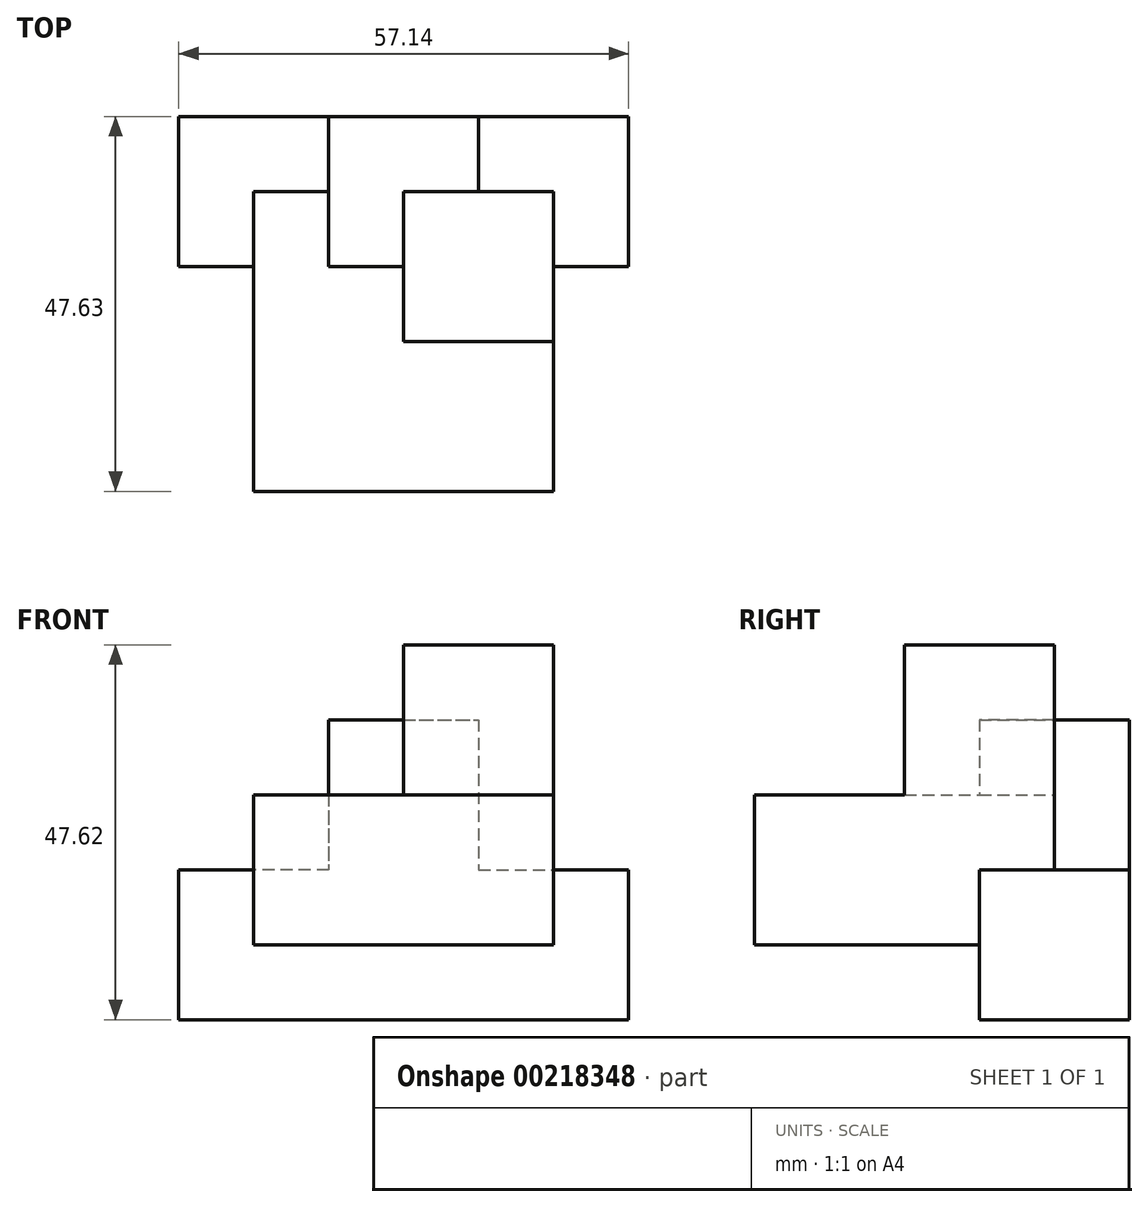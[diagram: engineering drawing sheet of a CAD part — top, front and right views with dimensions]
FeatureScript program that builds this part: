
annotation { "Feature Type Name" : "Feature", "Feature Type Description" : "" }
export const myFeature = defineFeature(function(context is Context, id is Id, definition is map)
    precondition{}
    {
        {
            var Q0;
            Q0=qCreatedBy(makeId("Front.planeOp"),FACE);
            var sketch = newSketch(context, id + "F0", { "sketchPlane" : qUnion([Q0])});
            skLineSegment(sketch, "E0.bottom", {"start": v(-9.52, 9.52) * mm, "end": v(9.53, 9.52) * mm});
            skLineSegment(sketch, "E0.top", {"start": v(-9.53, -9.53) * mm, "end": v(9.53, -9.53) * mm});
            skLineSegment(sketch, "E0.left", {"start": v(-9.53, 9.53) * mm, "end": v(-9.53, -9.53) * mm});
            skLineSegment(sketch, "E0.right", {"start": v(9.53, 9.53) * mm, "end": v(9.53, -9.53) * mm});
            skPoint(sketch, "E0.middle", {"position": v(0, 0) * mm});
            skLineSegment(sketch, "E1.bottom", {"start": v(-9.53, -9.53) * mm, "end": v(9.52, -9.53) * mm});
            skLineSegment(sketch, "E1.top", {"start": v(-9.53, -28.58) * mm, "end": v(9.53, -28.58) * mm});
            skLineSegment(sketch, "E1.left", {"start": v(-9.53, -9.53) * mm, "end": v(-9.53, -28.58) * mm});
            skLineSegment(sketch, "E1.right", {"start": v(9.52, -9.53) * mm, "end": v(9.52, -28.58) * mm});
            skLineSegment(sketch, "E2.bottom", {"start": v(-9.53, -9.53) * mm, "end": v(-28.58, -9.53) * mm});
            skLineSegment(sketch, "E2.top", {"start": v(-9.53, -28.58) * mm, "end": v(-28.57, -28.58) * mm});
            skLineSegment(sketch, "E2.right", {"start": v(-28.58, -9.53) * mm, "end": v(-28.57, -28.58) * mm});
            skLineSegment(sketch, "E3.bottom", {"start": v(9.53, -9.53) * mm, "end": v(28.57, -9.53) * mm});
            skLineSegment(sketch, "E3.top", {"start": v(9.53, -28.58) * mm, "end": v(28.57, -28.58) * mm});
            skLineSegment(sketch, "E3.left", {"start": v(9.53, -9.53) * mm, "end": v(9.53, -28.58) * mm});
            skLineSegment(sketch, "E3.right", {"start": v(28.57, -9.52) * mm, "end": v(28.57, -28.58) * mm});
            skSolve(sketch);
        }
        {
            var Q0;
            Q0=makeQuery(id+"F0.imprint","IMPRINT",FACE,{"disambiguationData":[TD([[makeQuery(id+"F0.imprint","IMPRINT",EDGE,{"derivedFrom":sQuery(id+"F0.wireOp",EDGE,"E0.bottom")}),-1.0]])]});
            var Q1;
            Q1=makeQuery(id+"F0.imprint","IMPRINT",FACE,{"disambiguationData":[TD([[makeQuery(id+"F0.imprint","IMPRINT",EDGE,{"derivedFrom":sQuery(id+"F0.wireOp",EDGE,"E2.bottom")}),1.0]])]});
            var Q2;
            Q2=makeQuery(id+"F0.imprint","IMPRINT",FACE,{"disambiguationData":[TD([[makeQuery(id+"F0.imprint","IMPRINT",EDGE,{"derivedFrom":sQuery(id+"F0.wireOp",EDGE,"E1.bottom")}),-1.0]])]});
            var Q3;
            Q3=makeQuery(id+"F0.imprint","IMPRINT",FACE,{"disambiguationData":[TD([[makeQuery(id+"F0.imprint","IMPRINT",EDGE,{"derivedFrom":sQuery(id+"F0.wireOp",EDGE,"E3.bottom")}),-1.0]])]});
            extrude(context, id + "F1", {"entities" : qUnion([Q0, Q1, Q2, Q3]), "endBound" : BoundingType.SYMMETRIC, "depth" : 19.05 * mm});
        }
        {
            var Q0;
            Q0=qCreatedBy(makeId("Front.planeOp"),FACE);
            var sketch = newSketch(context, id + "F2", { "sketchPlane" : qUnion([Q0])});
            skLineSegment(sketch, "E4.bottom", {"start": v(0, 0) * mm, "end": v(-19.05, 0) * mm});
            skLineSegment(sketch, "E4.left", {"start": v(0, 0) * mm, "end": v(0, 19.05) * mm});
            skLineSegment(sketch, "E5.top", {"start": v(0, -19.05) * mm, "end": v(-19.05, -19.05) * mm});
            skLineSegment(sketch, "E5.left", {"start": v(0, 0) * mm, "end": v(0, -19.05) * mm});
            skLineSegment(sketch, "E5.right", {"start": v(-19.05, 0) * mm, "end": v(-19.05, -19.05) * mm});
            skLineSegment(sketch, "E6.bottom", {"start": v(0, 0) * mm, "end": v(19.05, 0) * mm});
            skLineSegment(sketch, "E6.top", {"start": v(0, 19.05) * mm, "end": v(19.05, 19.05) * mm});
            skLineSegment(sketch, "E6.right", {"start": v(19.05, 0) * mm, "end": v(19.05, 19.05) * mm});
            skLineSegment(sketch, "E7.top", {"start": v(0, -19.05) * mm, "end": v(19.05, -19.05) * mm});
            skLineSegment(sketch, "E7.right", {"start": v(19.05, 0) * mm, "end": v(19.05, -19.05) * mm});
            skSolve(sketch);
        }
        {
            var Q0;
            Q0=makeQuery(id+"F2.imprint","IMPRINT",FACE,{"disambiguationData":[TD([[makeQuery(id+"F2.imprint","IMPRINT",EDGE,{"derivedFrom":sQuery(id+"F2.wireOp",EDGE,"E4.bottom")}),1.0]])]});
            var Q1;
            Q1=makeQuery(id+"F2.imprint","IMPRINT",FACE,{"disambiguationData":[TD([[makeQuery(id+"F2.imprint","IMPRINT",EDGE,{"derivedFrom":sQuery(id+"F2.wireOp",EDGE,"E6.bottom")}),-1.0]])]});
            extrude(context, id + "F3", {"entities" : qUnion([Q0, Q1]), "depth" : 38.1 * mm});
        }
        {
            var Q0;
            Q0 = qSketchRegion(id + "F2", true);
            extrude(context, id + "F4", {"entities" : qUnion([Q0]), "operationType" : NewBodyOperationType.ADD, "depth" : 19.05 * mm});
        }
    });
